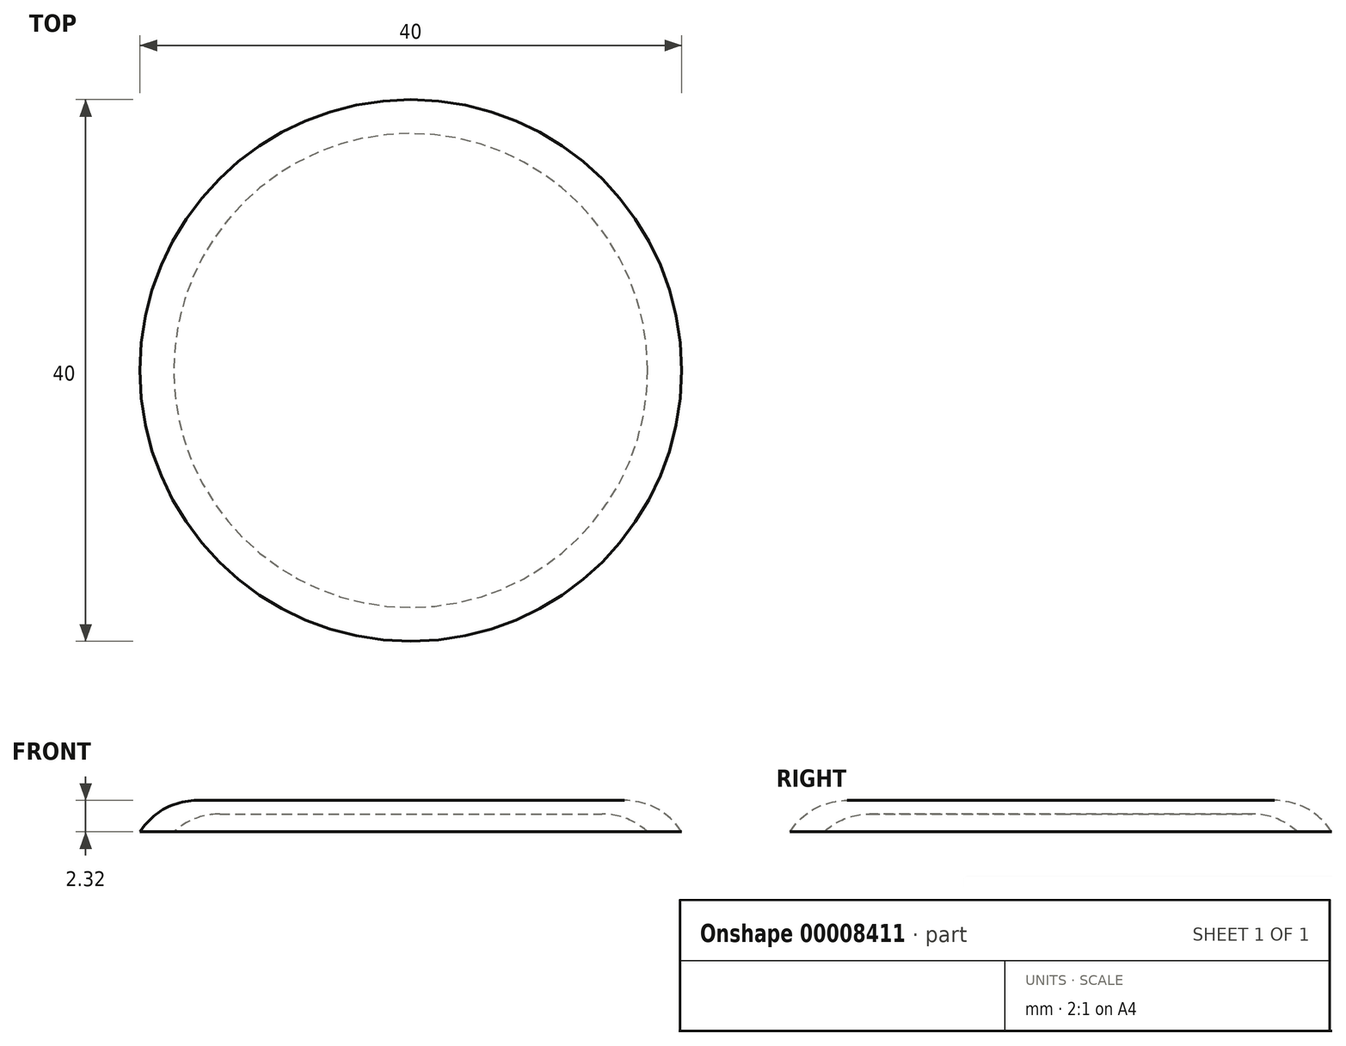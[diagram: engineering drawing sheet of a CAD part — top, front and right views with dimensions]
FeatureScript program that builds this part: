
annotation { "Feature Type Name" : "Feature", "Feature Type Description" : "" }
export const myFeature = defineFeature(function(context is Context, id is Id, definition is map)
    precondition{}
    {
        {
            var Q0;
            Q0=qCreatedBy(makeId("Front.planeOp"),FACE);
            var sketch = newSketch(context, id + "F0", { "sketchPlane" : qUnion([Q0])});
            skLineSegment(sketch, "E0", {"start": v(0, 0) * mm, "end": v(15.78, 0) * mm});
            skLineSegment(sketch, "E1", {"start": v(20.78, -5) * mm, "end": v(20.78, -5) * mm});
            skLineSegment(sketch, "E2", {"start": v(14.12, -1) * mm, "end": v(0, -1) * mm});
            skLineSegment(sketch, "E3", {"start": v(0, -1) * mm, "end": v(0, 0) * mm});
            skPoint(sketch, "E4.visualSharp", {"position": v(20.78, 0) * mm});
            skArc(sketch, "E4.filletArc", {"start": v(20, -2.32) * mm, "mid": v(18.19, -0.62) * mm, "end": v(15.78, 0) * mm});
            skPoint(sketch, "E5.visualSharp", {"position": v(17.5, -1) * mm});
            skArc(sketch, "E5.filletArc", {"start": v(17.5, -2.32) * mm, "mid": v(15.93, -1.34) * mm, "end": v(14.12, -1) * mm});
            skLineSegment(sketch, "E6", {"start": v(20, -2.32) * mm, "end": v(17.5, -2.32) * mm});
            skSolve(sketch);
        }
        {
            var Q0;
            Q0 = qSketchRegion(id + "F0", true);
            var Q1;
            Q1=sQuery(id+"F0.wireOp",EDGE,"E3");
            revolve(context, id + "F1", {"entities" : qUnion([Q0]), "axis" : qUnion([Q1]), "revolveType" : RevolveType.FULL});
        }
    });
